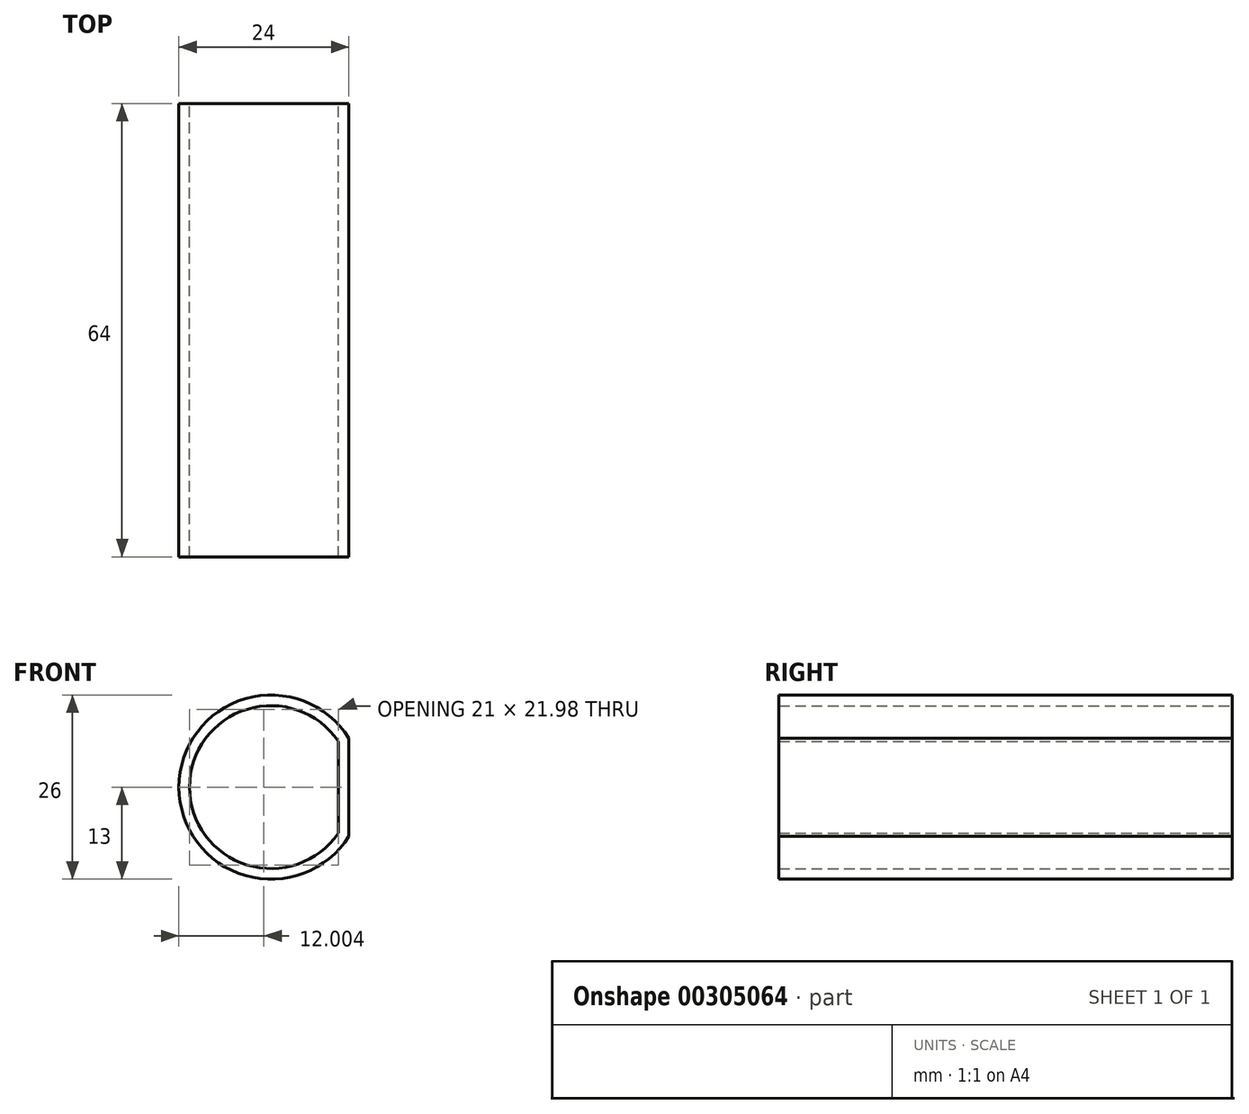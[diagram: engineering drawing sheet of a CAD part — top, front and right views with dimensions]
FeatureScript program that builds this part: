
annotation { "Feature Type Name" : "Feature", "Feature Type Description" : "" }
export const myFeature = defineFeature(function(context is Context, id is Id, definition is map)
    precondition{}
    {
        {
            var Q0;
            Q0=qCreatedBy(makeId("Front.planeOp"),FACE);
            var sketch = newSketch(context, id + "F0", { "sketchPlane" : qUnion([Q0])});
            skArc(sketch, "E0", {"start": v(10.51, 6.52) * mm, "mid": v(-13.49, -0.4) * mm, "end": v(10.51, -7.34) * mm});
            skLineSegment(sketch, "E1", {"start": v(10.51, 6.52) * mm, "end": v(10.51, -7.34) * mm});
            skPoint(sketch, "E2", {"position": v(-13.32, 1.64) * mm});
            skArc(sketch, "E3.0", {"start": v(9.01, 6.07) * mm, "mid": v(-11.99, -0.4) * mm, "end": v(9.01, -6.9) * mm});
            skLineSegment(sketch, "E3.1", {"start": v(9.01, 6.07) * mm, "end": v(9.01, -6.9) * mm});
            skSolve(sketch);
        }
        {
            var Q0;
            Q0 = qSketchRegion(id + "F0", true);
            extrude(context, id + "F1", {"entities" : qUnion([Q0]), "depth" : 64 * mm});
        }
    });
